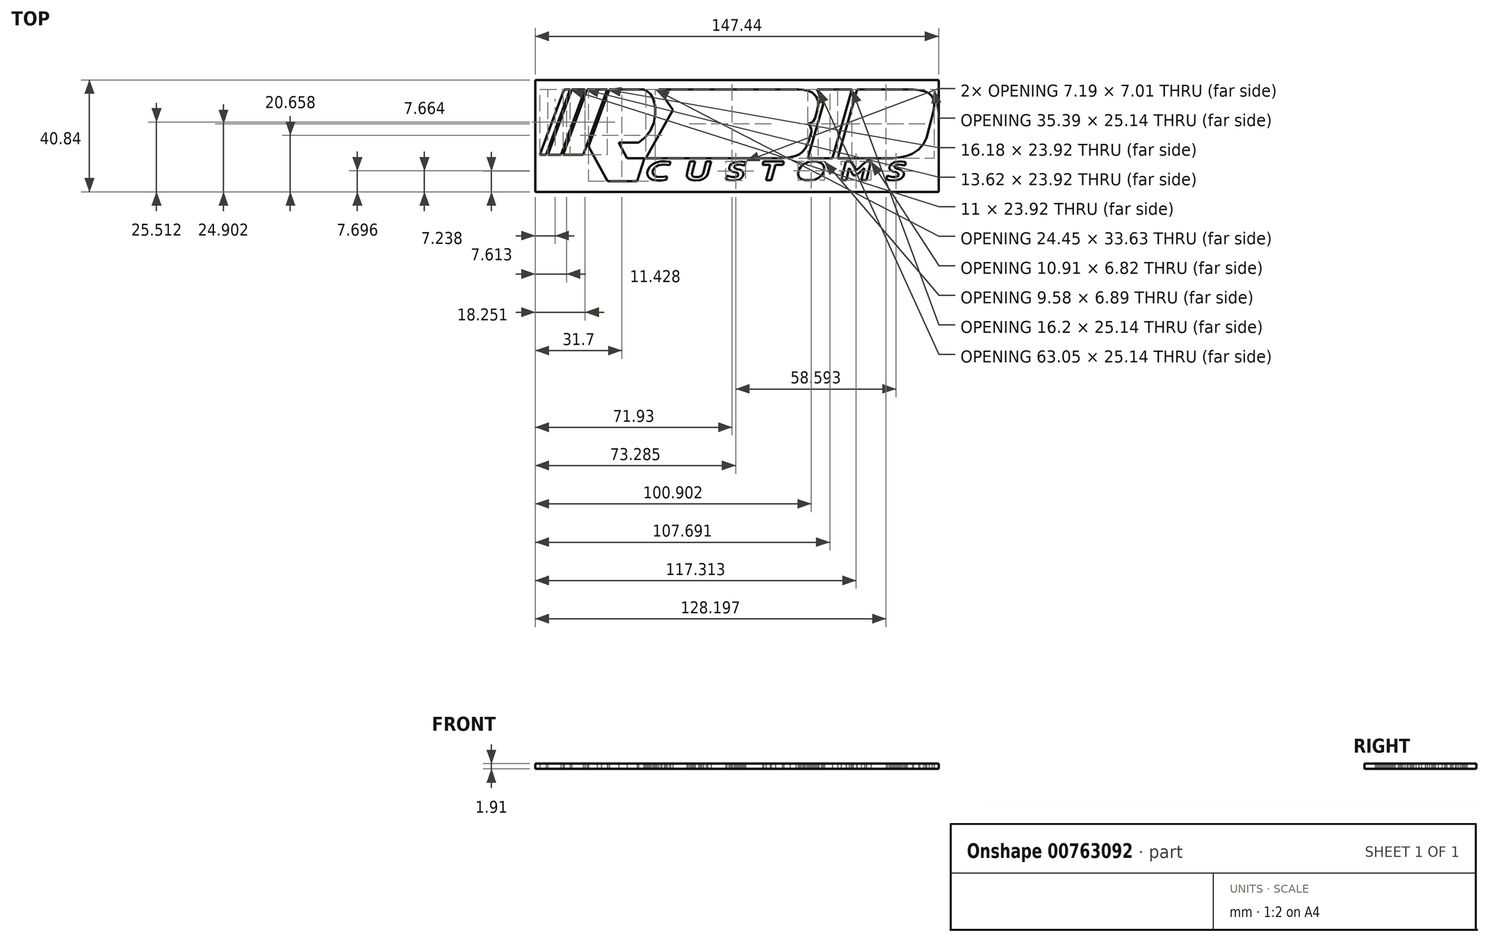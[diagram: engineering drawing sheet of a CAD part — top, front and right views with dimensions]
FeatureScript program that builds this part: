
annotation { "Feature Type Name" : "Feature", "Feature Type Description" : "" }
export const myFeature = defineFeature(function(context is Context, id is Id, definition is map)
    precondition{}
    {
        {
            var Q0;
            Q0=qCreatedBy(makeId("Top.planeOp"),FACE);
            var sketch = newSketch(context, id + "F0", { "sketchPlane" : qUnion([Q0])});
            skLineSegment(sketch, "E0", {"start": v(40.42, -9.55) * mm, "end": v(42.26, -9.55) * mm});
            skLineSegment(sketch, "E1", {"start": v(46.05, -16.37) * mm, "end": v(47.89, -16.37) * mm});
            skLineSegment(sketch, "E2", {"start": v(47.82, -9.55) * mm, "end": v(49.6, -9.55) * mm});
            skLineSegment(sketch, "E3", {"start": v(47.16, -11.96) * mm, "end": v(46.05, -16.37) * mm});
            skLineSegment(sketch, "E4", {"start": v(44.27, -14.59) * mm, "end": v(47.16, -11.96) * mm});
            skLineSegment(sketch, "E5", {"start": v(43.16, -14.59) * mm, "end": v(44.27, -14.59) * mm});
            skLineSegment(sketch, "E6", {"start": v(41.6, -11.98) * mm, "end": v(43.16, -14.59) * mm});
            skLineSegment(sketch, "E7", {"start": v(49.6, -9.55) * mm, "end": v(47.89, -16.37) * mm});
            skLineSegment(sketch, "E8", {"start": v(44.21, -12.83) * mm, "end": v(47.82, -9.55) * mm});
            skLineSegment(sketch, "E9", {"start": v(42.26, -9.55) * mm, "end": v(44.21, -12.83) * mm});
            skLineSegment(sketch, "E10", {"start": v(41.6, -11.98) * mm, "end": v(40.5, -16.37) * mm});
            skLineSegment(sketch, "E11", {"start": v(40.42, -9.55) * mm, "end": v(38.7, -16.37) * mm});
            skLineSegment(sketch, "E12", {"start": v(28.33, -9.55) * mm, "end": v(26.64, -9.76) * mm});
            skLineSegment(sketch, "E13", {"start": v(26.64, -9.76) * mm, "end": v(24.97, -10.5) * mm});
            skLineSegment(sketch, "E14", {"start": v(24.97, -10.5) * mm, "end": v(23.75, -11.65) * mm});
            skLineSegment(sketch, "E15", {"start": v(23.75, -11.65) * mm, "end": v(23.18, -12.71) * mm});
            skLineSegment(sketch, "E16", {"start": v(23.18, -12.71) * mm, "end": v(22.95, -13.91) * mm});
            skLineSegment(sketch, "E17", {"start": v(22.95, -13.91) * mm, "end": v(23.15, -15.07) * mm});
            skLineSegment(sketch, "E18", {"start": v(23.15, -15.07) * mm, "end": v(23.88, -15.86) * mm});
            skLineSegment(sketch, "E19", {"start": v(23.88, -15.86) * mm, "end": v(25.38, -16.36) * mm});
            skLineSegment(sketch, "E20", {"start": v(25.38, -16.36) * mm, "end": v(27.12, -16.44) * mm});
            skLineSegment(sketch, "E21", {"start": v(27.12, -16.44) * mm, "end": v(28.98, -16.25) * mm});
            skLineSegment(sketch, "E22", {"start": v(28.98, -16.25) * mm, "end": v(30.55, -15.5) * mm});
            skLineSegment(sketch, "E23", {"start": v(30.55, -15.5) * mm, "end": v(31.72, -14.43) * mm});
            skLineSegment(sketch, "E24", {"start": v(31.72, -14.43) * mm, "end": v(32.25, -13.43) * mm});
            skLineSegment(sketch, "E25", {"start": v(32.25, -13.43) * mm, "end": v(32.53, -12.09) * mm});
            skLineSegment(sketch, "E26", {"start": v(32.53, -12.09) * mm, "end": v(32.23, -10.87) * mm});
            skLineSegment(sketch, "E27", {"start": v(32.23, -10.87) * mm, "end": v(31.4, -10.13) * mm});
            skLineSegment(sketch, "E28", {"start": v(31.4, -10.13) * mm, "end": v(29.92, -9.63) * mm});
            skLineSegment(sketch, "E29", {"start": v(29.92, -9.63) * mm, "end": v(28.33, -9.55) * mm});
            skLineSegment(sketch, "E30", {"start": v(17.42, -10.84) * mm, "end": v(17.74, -9.55) * mm});
            skLineSegment(sketch, "E31", {"start": v(14.63, -10.84) * mm, "end": v(17.42, -10.84) * mm});
            skLineSegment(sketch, "E32", {"start": v(13.16, -16.37) * mm, "end": v(14.63, -10.84) * mm});
            skLineSegment(sketch, "E33", {"start": v(11.28, -16.37) * mm, "end": v(11.47, -16.37) * mm});
            skLineSegment(sketch, "E34", {"start": v(12.75, -10.84) * mm, "end": v(11.28, -16.37) * mm});
            skLineSegment(sketch, "E35", {"start": v(9.96, -10.84) * mm, "end": v(12.75, -10.84) * mm});
            skLineSegment(sketch, "E36", {"start": v(10.28, -9.55) * mm, "end": v(9.96, -10.84) * mm});
            skLineSegment(sketch, "E37", {"start": v(55.5, -14.69) * mm, "end": v(55.12, -16.02) * mm});
            skLineSegment(sketch, "E38", {"start": v(62.31, -9.82) * mm, "end": v(60.42, -9.53) * mm});
            skLineSegment(sketch, "E39", {"start": v(60.42, -9.53) * mm, "end": v(58.37, -9.72) * mm});
            skLineSegment(sketch, "E40", {"start": v(58.37, -9.72) * mm, "end": v(56.95, -10.49) * mm});
            skLineSegment(sketch, "E41", {"start": v(56.95, -10.49) * mm, "end": v(56.44, -11.2) * mm});
            skLineSegment(sketch, "E42", {"start": v(56.44, -11.2) * mm, "end": v(56.3, -12.06) * mm});
            skLineSegment(sketch, "E43", {"start": v(56.3, -12.06) * mm, "end": v(56.52, -12.6) * mm});
            skLineSegment(sketch, "E44", {"start": v(56.52, -12.6) * mm, "end": v(57.02, -12.95) * mm});
            skLineSegment(sketch, "E45", {"start": v(57.02, -12.95) * mm, "end": v(57.56, -13.17) * mm});
            skLineSegment(sketch, "E46", {"start": v(57.56, -13.17) * mm, "end": v(58.24, -13.4) * mm});
            skLineSegment(sketch, "E47", {"start": v(58.24, -13.4) * mm, "end": v(58.94, -13.62) * mm});
            skLineSegment(sketch, "E48", {"start": v(58.94, -13.62) * mm, "end": v(59.4, -13.82) * mm});
            skLineSegment(sketch, "E49", {"start": v(59.4, -13.82) * mm, "end": v(59.67, -14.18) * mm});
            skLineSegment(sketch, "E50", {"start": v(59.67, -14.18) * mm, "end": v(59.68, -14.56) * mm});
            skLineSegment(sketch, "E51", {"start": v(59.68, -14.56) * mm, "end": v(59.34, -14.98) * mm});
            skLineSegment(sketch, "E52", {"start": v(59.34, -14.98) * mm, "end": v(58.5, -15.25) * mm});
            skLineSegment(sketch, "E53", {"start": v(58.5, -15.25) * mm, "end": v(57.48, -15.22) * mm});
            skLineSegment(sketch, "E54", {"start": v(57.48, -15.22) * mm, "end": v(56.34, -15.01) * mm});
            skLineSegment(sketch, "E55", {"start": v(56.34, -15.01) * mm, "end": v(55.5, -14.69) * mm});
            skLineSegment(sketch, "E56", {"start": v(62.05, -11.04) * mm, "end": v(60.8, -10.76) * mm});
            skLineSegment(sketch, "E57", {"start": v(60.8, -10.76) * mm, "end": v(59.61, -10.67) * mm});
            skLineSegment(sketch, "E58", {"start": v(59.61, -10.67) * mm, "end": v(58.6, -10.88) * mm});
            skLineSegment(sketch, "E59", {"start": v(58.6, -10.88) * mm, "end": v(58.19, -11.37) * mm});
            skLineSegment(sketch, "E60", {"start": v(58.19, -11.37) * mm, "end": v(58.28, -11.84) * mm});
            skLineSegment(sketch, "E61", {"start": v(58.28, -11.84) * mm, "end": v(58.79, -12.13) * mm});
            skLineSegment(sketch, "E62", {"start": v(58.79, -12.13) * mm, "end": v(59.58, -12.38) * mm});
            skLineSegment(sketch, "E63", {"start": v(59.58, -12.38) * mm, "end": v(60.29, -12.61) * mm});
            skLineSegment(sketch, "E64", {"start": v(60.29, -12.61) * mm, "end": v(60.77, -12.83) * mm});
            skLineSegment(sketch, "E65", {"start": v(60.77, -12.83) * mm, "end": v(61.5, -13.41) * mm});
            skLineSegment(sketch, "E66", {"start": v(61.5, -13.41) * mm, "end": v(61.6, -14.2) * mm});
            skLineSegment(sketch, "E67", {"start": v(61.6, -14.2) * mm, "end": v(61.33, -15.03) * mm});
            skLineSegment(sketch, "E68", {"start": v(61.33, -15.03) * mm, "end": v(60.68, -15.74) * mm});
            skLineSegment(sketch, "E69", {"start": v(60.68, -15.74) * mm, "end": v(59.85, -16.19) * mm});
            skLineSegment(sketch, "E70", {"start": v(59.85, -16.19) * mm, "end": v(58.8, -16.44) * mm});
            skLineSegment(sketch, "E71", {"start": v(58.8, -16.44) * mm, "end": v(57.5, -16.54) * mm});
            skLineSegment(sketch, "E72", {"start": v(57.5, -16.54) * mm, "end": v(56.2, -16.35) * mm});
            skLineSegment(sketch, "E73", {"start": v(56.2, -16.35) * mm, "end": v(55.12, -16.02) * mm});
            skLineSegment(sketch, "E74", {"start": v(62.31, -9.82) * mm, "end": v(62.05, -11.04) * mm});
            skLineSegment(sketch, "E75", {"start": v(-3.1, -14.7) * mm, "end": v(-3.47, -16.03) * mm});
            skLineSegment(sketch, "E76", {"start": v(3.72, -9.83) * mm, "end": v(1.82, -9.54) * mm});
            skLineSegment(sketch, "E77", {"start": v(1.82, -9.54) * mm, "end": v(-0.22, -9.73) * mm});
            skLineSegment(sketch, "E78", {"start": v(-0.22, -9.73) * mm, "end": v(-1.65, -10.5) * mm});
            skLineSegment(sketch, "E79", {"start": v(-1.65, -10.5) * mm, "end": v(-2.15, -11.2) * mm});
            skLineSegment(sketch, "E80", {"start": v(-2.15, -11.2) * mm, "end": v(-2.3, -12.06) * mm});
            skLineSegment(sketch, "E81", {"start": v(-2.3, -12.06) * mm, "end": v(-2.07, -12.61) * mm});
            skLineSegment(sketch, "E82", {"start": v(-2.07, -12.61) * mm, "end": v(-1.57, -12.96) * mm});
            skLineSegment(sketch, "E83", {"start": v(-1.57, -12.96) * mm, "end": v(-1.04, -13.18) * mm});
            skLineSegment(sketch, "E84", {"start": v(-1.04, -13.18) * mm, "end": v(-0.35, -13.4) * mm});
            skLineSegment(sketch, "E85", {"start": v(-0.35, -13.4) * mm, "end": v(0.34, -13.63) * mm});
            skLineSegment(sketch, "E86", {"start": v(0.34, -13.63) * mm, "end": v(0.8, -13.83) * mm});
            skLineSegment(sketch, "E87", {"start": v(0.8, -13.83) * mm, "end": v(1.08, -14.19) * mm});
            skLineSegment(sketch, "E88", {"start": v(1.08, -14.19) * mm, "end": v(1.08, -14.57) * mm});
            skLineSegment(sketch, "E89", {"start": v(1.08, -14.57) * mm, "end": v(0.75, -15) * mm});
            skLineSegment(sketch, "E90", {"start": v(0.75, -15) * mm, "end": v(-0.1, -15.26) * mm});
            skLineSegment(sketch, "E91", {"start": v(-0.1, -15.26) * mm, "end": v(-1.11, -15.23) * mm});
            skLineSegment(sketch, "E92", {"start": v(-1.11, -15.23) * mm, "end": v(-2.25, -15.02) * mm});
            skLineSegment(sketch, "E93", {"start": v(-2.25, -15.02) * mm, "end": v(-3.1, -14.7) * mm});
            skLineSegment(sketch, "E94", {"start": v(3.46, -11.04) * mm, "end": v(2.2, -10.77) * mm});
            skLineSegment(sketch, "E95", {"start": v(2.2, -10.77) * mm, "end": v(1.02, -10.68) * mm});
            skLineSegment(sketch, "E96", {"start": v(1.02, -10.68) * mm, "end": v(0.02, -10.89) * mm});
            skLineSegment(sketch, "E97", {"start": v(0.02, -10.89) * mm, "end": v(-0.4, -11.38) * mm});
            skLineSegment(sketch, "E98", {"start": v(-0.4, -11.38) * mm, "end": v(-0.31, -11.85) * mm});
            skLineSegment(sketch, "E99", {"start": v(-0.31, -11.85) * mm, "end": v(0.2, -12.14) * mm});
            skLineSegment(sketch, "E100", {"start": v(0.2, -12.14) * mm, "end": v(0.99, -12.4) * mm});
            skLineSegment(sketch, "E101", {"start": v(0.99, -12.4) * mm, "end": v(1.7, -12.62) * mm});
            skLineSegment(sketch, "E102", {"start": v(1.7, -12.62) * mm, "end": v(2.18, -12.84) * mm});
            skLineSegment(sketch, "E103", {"start": v(2.18, -12.84) * mm, "end": v(2.9, -13.42) * mm});
            skLineSegment(sketch, "E104", {"start": v(2.9, -13.42) * mm, "end": v(3, -14.21) * mm});
            skLineSegment(sketch, "E105", {"start": v(3, -14.21) * mm, "end": v(2.73, -15.04) * mm});
            skLineSegment(sketch, "E106", {"start": v(2.73, -15.04) * mm, "end": v(2.08, -15.75) * mm});
            skLineSegment(sketch, "E107", {"start": v(2.08, -15.75) * mm, "end": v(1.25, -16.2) * mm});
            skLineSegment(sketch, "E108", {"start": v(1.25, -16.2) * mm, "end": v(0.2, -16.45) * mm});
            skLineSegment(sketch, "E109", {"start": v(0.2, -16.45) * mm, "end": v(-1.08, -16.55) * mm});
            skLineSegment(sketch, "E110", {"start": v(-1.08, -16.55) * mm, "end": v(-2.4, -16.36) * mm});
            skLineSegment(sketch, "E111", {"start": v(-2.4, -16.36) * mm, "end": v(-3.47, -16.03) * mm});
            skLineSegment(sketch, "E112", {"start": v(3.72, -9.83) * mm, "end": v(3.46, -11.04) * mm});
            skLineSegment(sketch, "E113", {"start": v(-10.66, -9.55) * mm, "end": v(-8.86, -9.55) * mm});
            skLineSegment(sketch, "E114", {"start": v(-15.84, -13.84) * mm, "end": v(-15.9, -14.3) * mm});
            skLineSegment(sketch, "E115", {"start": v(-15.9, -14.3) * mm, "end": v(-15.74, -14.76) * mm});
            skLineSegment(sketch, "E116", {"start": v(-15.74, -14.76) * mm, "end": v(-15.37, -15.07) * mm});
            skLineSegment(sketch, "E117", {"start": v(-15.37, -15.07) * mm, "end": v(-14.82, -15.24) * mm});
            skLineSegment(sketch, "E118", {"start": v(-14.82, -15.24) * mm, "end": v(-13.42, -15.23) * mm});
            skLineSegment(sketch, "E119", {"start": v(-13.42, -15.23) * mm, "end": v(-12.35, -14.87) * mm});
            skLineSegment(sketch, "E120", {"start": v(-12.35, -14.87) * mm, "end": v(-11.82, -14.03) * mm});
            skLineSegment(sketch, "E121", {"start": v(-17.67, -13.74) * mm, "end": v(-17.74, -14.84) * mm});
            skLineSegment(sketch, "E122", {"start": v(-17.74, -14.84) * mm, "end": v(-17.26, -15.76) * mm});
            skLineSegment(sketch, "E123", {"start": v(-17.26, -15.76) * mm, "end": v(-16.24, -16.3) * mm});
            skLineSegment(sketch, "E124", {"start": v(-16.24, -16.3) * mm, "end": v(-14.86, -16.5) * mm});
            skLineSegment(sketch, "E125", {"start": v(-14.86, -16.5) * mm, "end": v(-12.9, -16.4) * mm});
            skLineSegment(sketch, "E126", {"start": v(-12.9, -16.4) * mm, "end": v(-11.66, -15.9) * mm});
            skLineSegment(sketch, "E127", {"start": v(-11.66, -15.9) * mm, "end": v(-10.58, -15.08) * mm});
            skLineSegment(sketch, "E128", {"start": v(-10.58, -15.08) * mm, "end": v(-10.05, -14.17) * mm});
            skLineSegment(sketch, "E129", {"start": v(-8.86, -9.55) * mm, "end": v(-10.05, -14.17) * mm});
            skLineSegment(sketch, "E130", {"start": v(-10.66, -9.55) * mm, "end": v(-11.82, -14.03) * mm});
            skLineSegment(sketch, "E131", {"start": v(-14.73, -9.55) * mm, "end": v(-15.84, -13.84) * mm});
            skLineSegment(sketch, "E132", {"start": v(-16.58, -9.55) * mm, "end": v(-17.67, -13.74) * mm});
            skLineSegment(sketch, "E133", {"start": v(11.47, -16.37) * mm, "end": v(13.16, -16.37) * mm});
            skLineSegment(sketch, "E134", {"start": v(-16.58, -9.55) * mm, "end": v(-14.73, -9.55) * mm});
            skLineSegment(sketch, "E135", {"start": v(-24.91, -15.04) * mm, "end": v(-25.17, -16.21) * mm});
            skLineSegment(sketch, "E136", {"start": v(-23.75, -9.7) * mm, "end": v(-25.46, -9.49) * mm});
            skLineSegment(sketch, "E137", {"start": v(-25.46, -9.49) * mm, "end": v(-27.31, -9.52) * mm});
            skLineSegment(sketch, "E138", {"start": v(-27.31, -9.52) * mm, "end": v(-29.2, -10.02) * mm});
            skLineSegment(sketch, "E139", {"start": v(-29.2, -10.02) * mm, "end": v(-30.33, -10.61) * mm});
            skLineSegment(sketch, "E140", {"start": v(-30.33, -10.61) * mm, "end": v(-31.37, -11.6) * mm});
            skLineSegment(sketch, "E141", {"start": v(-31.37, -11.6) * mm, "end": v(-31.97, -12.67) * mm});
            skLineSegment(sketch, "E142", {"start": v(-31.97, -12.67) * mm, "end": v(-32.2, -13.7) * mm});
            skLineSegment(sketch, "E143", {"start": v(-32.2, -13.7) * mm, "end": v(-32.1, -14.5) * mm});
            skLineSegment(sketch, "E144", {"start": v(-32.1, -14.5) * mm, "end": v(-31.75, -15.24) * mm});
            skLineSegment(sketch, "E145", {"start": v(-31.75, -15.24) * mm, "end": v(-31.15, -15.81) * mm});
            skLineSegment(sketch, "E146", {"start": v(-31.15, -15.81) * mm, "end": v(-30.33, -16.2) * mm});
            skLineSegment(sketch, "E147", {"start": v(-30.33, -16.2) * mm, "end": v(-28.66, -16.51) * mm});
            skLineSegment(sketch, "E148", {"start": v(-28.66, -16.51) * mm, "end": v(-26.83, -16.51) * mm});
            skLineSegment(sketch, "E149", {"start": v(-26.83, -16.51) * mm, "end": v(-25.17, -16.21) * mm});
            skLineSegment(sketch, "E150", {"start": v(-24.03, -10.99) * mm, "end": v(-26.03, -10.68) * mm});
            skLineSegment(sketch, "E151", {"start": v(-26.03, -10.68) * mm, "end": v(-28.04, -10.96) * mm});
            skLineSegment(sketch, "E152", {"start": v(-28.04, -10.96) * mm, "end": v(-29.02, -11.46) * mm});
            skLineSegment(sketch, "E153", {"start": v(-29.02, -11.46) * mm, "end": v(-29.77, -12.2) * mm});
            skLineSegment(sketch, "E154", {"start": v(-29.77, -12.2) * mm, "end": v(-30.16, -12.97) * mm});
            skLineSegment(sketch, "E155", {"start": v(-30.16, -12.97) * mm, "end": v(-30.23, -13.75) * mm});
            skLineSegment(sketch, "E156", {"start": v(-30.23, -13.75) * mm, "end": v(-29.78, -14.65) * mm});
            skLineSegment(sketch, "E157", {"start": v(-29.78, -14.65) * mm, "end": v(-28.8, -15.1) * mm});
            skLineSegment(sketch, "E158", {"start": v(-28.8, -15.1) * mm, "end": v(-26.94, -15.3) * mm});
            skLineSegment(sketch, "E159", {"start": v(-26.94, -15.3) * mm, "end": v(-24.91, -15.04) * mm});
            skLineSegment(sketch, "E160", {"start": v(-23.75, -9.7) * mm, "end": v(-24.03, -10.99) * mm});
            skLineSegment(sketch, "E161", {"start": v(69.84, -0.9) * mm, "end": v(68.76, -3.12) * mm});
            skLineSegment(sketch, "E162", {"start": v(68.76, -3.12) * mm, "end": v(67, -5.17) * mm});
            skLineSegment(sketch, "E163", {"start": v(67, -5.17) * mm, "end": v(64.73, -6.7) * mm});
            skLineSegment(sketch, "E164", {"start": v(64.73, -6.7) * mm, "end": v(62.78, -7.48) * mm});
            skLineSegment(sketch, "E165", {"start": v(62.78, -7.48) * mm, "end": v(60.46, -8.02) * mm});
            skLineSegment(sketch, "E166", {"start": v(60.46, -8.02) * mm, "end": v(57.74, -8.33) * mm});
            skLineSegment(sketch, "E167", {"start": v(42.63, 16.81) * mm, "end": v(29.83, 16.81) * mm});
            skLineSegment(sketch, "E168", {"start": v(37.34, -8.33) * mm, "end": v(57.74, -8.33) * mm});
            skLineSegment(sketch, "E169", {"start": v(26.43, -8.33) * mm, "end": v(35.44, -8.33) * mm});
            skLineSegment(sketch, "E170", {"start": v(23.18, 16.81) * mm, "end": v(-0.77, 16.81) * mm});
            skLineSegment(sketch, "E171", {"start": v(-8.5, 16.81) * mm, "end": v(-28.07, 16.81) * mm});
            skLineSegment(sketch, "E172", {"start": v(2.73, -8.33) * mm, "end": v(17.25, -8.33) * mm});
            skLineSegment(sketch, "E173", {"start": v(-22.78, 9.31) * mm, "end": v(-32.76, -8.33) * mm});
            skLineSegment(sketch, "E174", {"start": v(29.83, 16.81) * mm, "end": v(32.18, 11.5) * mm});
            skLineSegment(sketch, "E175", {"start": v(32.18, 11.5) * mm, "end": v(26.43, -8.33) * mm});
            skLineSegment(sketch, "E176", {"start": v(42.63, 16.81) * mm, "end": v(35.44, -8.33) * mm});
            skLineSegment(sketch, "E177", {"start": v(44.53, 16.81) * mm, "end": v(37.34, -8.33) * mm});
            skLineSegment(sketch, "E178", {"start": v(72.6, 9.4) * mm, "end": v(72.73, 11.14) * mm});
            skLineSegment(sketch, "E179", {"start": v(72.73, 11.14) * mm, "end": v(72.5, 12.82) * mm});
            skLineSegment(sketch, "E180", {"start": v(72.5, 12.82) * mm, "end": v(71.77, 14.33) * mm});
            skLineSegment(sketch, "E181", {"start": v(71.77, 14.33) * mm, "end": v(70.74, 15.37) * mm});
            skLineSegment(sketch, "E182", {"start": v(70.74, 15.37) * mm, "end": v(69.33, 16.02) * mm});
            skLineSegment(sketch, "E183", {"start": v(69.33, 16.02) * mm, "end": v(67.4, 16.56) * mm});
            skLineSegment(sketch, "E184", {"start": v(67.4, 16.56) * mm, "end": v(65.13, 16.81) * mm});
            skLineSegment(sketch, "E185", {"start": v(72.6, 9.4) * mm, "end": v(69.84, -0.9) * mm});
            skLineSegment(sketch, "E186", {"start": v(26.33, 4.26) * mm, "end": v(27.18, 4.4) * mm});
            skLineSegment(sketch, "E187", {"start": v(27.18, 4.4) * mm, "end": v(27.93, 4.66) * mm});
            skLineSegment(sketch, "E188", {"start": v(27.93, 4.66) * mm, "end": v(28.5, 5.19) * mm});
            skLineSegment(sketch, "E189", {"start": v(28.5, 5.19) * mm, "end": v(29.07, 6.28) * mm});
            skLineSegment(sketch, "E190", {"start": v(29.07, 6.28) * mm, "end": v(29.82, 8.46) * mm});
            skLineSegment(sketch, "E191", {"start": v(29.82, 8.46) * mm, "end": v(30.3, 10.75) * mm});
            skLineSegment(sketch, "E192", {"start": v(30.3, 10.75) * mm, "end": v(30.27, 12.45) * mm});
            skLineSegment(sketch, "E193", {"start": v(30.27, 12.45) * mm, "end": v(29.52, 14.24) * mm});
            skLineSegment(sketch, "E194", {"start": v(29.52, 14.24) * mm, "end": v(28.06, 15.6) * mm});
            skLineSegment(sketch, "E195", {"start": v(28.06, 15.6) * mm, "end": v(26.62, 16.23) * mm});
            skLineSegment(sketch, "E196", {"start": v(26.62, 16.23) * mm, "end": v(24.88, 16.66) * mm});
            skLineSegment(sketch, "E197", {"start": v(24.88, 16.66) * mm, "end": v(23.18, 16.81) * mm});
            skLineSegment(sketch, "E198", {"start": v(26.33, 4.26) * mm, "end": v(26.98, 3.8) * mm});
            skLineSegment(sketch, "E199", {"start": v(26.98, 3.8) * mm, "end": v(27.5, 3.08) * mm});
            skLineSegment(sketch, "E200", {"start": v(27.5, 3.08) * mm, "end": v(27.8, 2.23) * mm});
            skLineSegment(sketch, "E201", {"start": v(27.8, 2.23) * mm, "end": v(27.8, 1.48) * mm});
            skLineSegment(sketch, "E202", {"start": v(27.8, 1.48) * mm, "end": v(27.47, 0.1) * mm});
            skLineSegment(sketch, "E203", {"start": v(27.47, 0.1) * mm, "end": v(26.82, -1.9) * mm});
            skLineSegment(sketch, "E204", {"start": v(26.82, -1.9) * mm, "end": v(26.2, -3.5) * mm});
            skLineSegment(sketch, "E205", {"start": v(26.2, -3.5) * mm, "end": v(25.56, -4.77) * mm});
            skLineSegment(sketch, "E206", {"start": v(25.56, -4.77) * mm, "end": v(24.6, -5.92) * mm});
            skLineSegment(sketch, "E207", {"start": v(24.6, -5.92) * mm, "end": v(23.49, -6.81) * mm});
            skLineSegment(sketch, "E208", {"start": v(23.49, -6.81) * mm, "end": v(22.2, -7.5) * mm});
            skLineSegment(sketch, "E209", {"start": v(22.2, -7.5) * mm, "end": v(19.95, -8) * mm});
            skLineSegment(sketch, "E210", {"start": v(19.95, -8) * mm, "end": v(17.25, -8.33) * mm});
            skLineSegment(sketch, "E211", {"start": v(-33.51, 16.81) * mm, "end": v(-32.12, 16.04) * mm});
            skLineSegment(sketch, "E212", {"start": v(-32.12, 16.04) * mm, "end": v(-30.97, 14.97) * mm});
            skLineSegment(sketch, "E213", {"start": v(-30.97, 14.97) * mm, "end": v(-30.1, 13.47) * mm});
            skLineSegment(sketch, "E214", {"start": v(-30.1, 13.47) * mm, "end": v(-29.23, 10.61) * mm});
            skLineSegment(sketch, "E215", {"start": v(-29.23, 10.61) * mm, "end": v(-29.24, 7.62) * mm});
            skLineSegment(sketch, "E216", {"start": v(-29.24, 7.62) * mm, "end": v(-29.86, 4.52) * mm});
            skLineSegment(sketch, "E217", {"start": v(-29.86, 4.52) * mm, "end": v(-31.1, 1.59) * mm});
            skLineSegment(sketch, "E218", {"start": v(-31.1, 1.59) * mm, "end": v(-33.02, -0.8) * mm});
            skLineSegment(sketch, "E219", {"start": v(-33.02, -0.8) * mm, "end": v(-35.37, -2.66) * mm});
            skLineSegment(sketch, "E220", {"start": v(-33.51, 16.81) * mm, "end": v(-46.1, 16.81) * mm});
            skLineSegment(sketch, "E221", {"start": v(-5.07, -8.33) * mm, "end": v(2.3, -8.33) * mm});
            skLineSegment(sketch, "E222", {"start": v(38.7, -16.37) * mm, "end": v(40.5, -16.37) * mm});
            skLineSegment(sketch, "E223", {"start": v(28.33, -9.55) * mm, "end": v(29.1, -9.55) * mm});
            skLineSegment(sketch, "E224", {"start": v(10.28, -9.55) * mm, "end": v(17.74, -9.55) * mm});
            skLineSegment(sketch, "E225", {"start": v(1.03, -9.55) * mm, "end": v(2.06, -9.55) * mm});
            skLineSegment(sketch, "E226", {"start": v(65.13, 16.81) * mm, "end": v(44.53, 16.81) * mm});
            skLineSegment(sketch, "E227", {"start": v(-49, 8.95) * mm, "end": v(-46.1, 16.81) * mm});
            skLineSegment(sketch, "E228", {"start": v(-50.53, 4.54) * mm, "end": v(-53.69, -4.04) * mm});
            skLineSegment(sketch, "E229", {"start": v(-53.69, -4.04) * mm, "end": v(-46.73, -16.81) * mm});
            skLineSegment(sketch, "E230", {"start": v(-46.73, -16.81) * mm, "end": v(-35.85, -16.81) * mm});
            skLineSegment(sketch, "E231", {"start": v(-35.85, -16.81) * mm, "end": v(-33.28, -8.33) * mm});
            skLineSegment(sketch, "E232", {"start": v(-33.28, -8.33) * mm, "end": v(-39.56, -8.33) * mm});
            skLineSegment(sketch, "E233", {"start": v(-39.56, -8.33) * mm, "end": v(-42.64, -2.66) * mm});
            skLineSegment(sketch, "E234", {"start": v(-42.64, -2.66) * mm, "end": v(-35.37, -2.66) * mm});
            skLineSegment(sketch, "E235", {"start": v(-32.76, -8.33) * mm, "end": v(-22.07, -8.33) * mm});
            skLineSegment(sketch, "E236", {"start": v(-28.07, 16.81) * mm, "end": v(-22.78, 9.31) * mm});
            skLineSegment(sketch, "E237", {"start": v(-22.07, -8.33) * mm, "end": v(-5.07, -8.33) * mm});
            skLineSegment(sketch, "E238", {"start": v(-49, 8.95) * mm, "end": v(-50.53, 4.54) * mm});
            skLineSegment(sketch, "E239", {"start": v(-8.5, 16.81) * mm, "end": v(-0.77, 16.81) * mm});
            skLineSegment(sketch, "E240", {"start": v(2.3, -8.33) * mm, "end": v(2.73, -8.33) * mm});
            skLineSegment(sketch, "E241", {"start": v(-71.42, -7.1) * mm, "end": v(-62.62, 16.81) * mm});
            skLineSegment(sketch, "E242", {"start": v(-55.62, -7.1) * mm, "end": v(-63, -7.1) * mm});
            skLineSegment(sketch, "E243", {"start": v(-60.42, 16.81) * mm, "end": v(-69.22, -7.1) * mm});
            skLineSegment(sketch, "E244", {"start": v(-68.54, -7.1) * mm, "end": v(-59.74, 16.81) * mm});
            skLineSegment(sketch, "E245", {"start": v(-54.92, 16.81) * mm, "end": v(-63.73, -7.1) * mm});
            skLineSegment(sketch, "E246", {"start": v(-63, -7.1) * mm, "end": v(-54.2, 16.81) * mm});
            skLineSegment(sketch, "E247", {"start": v(-46.82, 16.81) * mm, "end": v(-55.62, -7.1) * mm});
            skLineSegment(sketch, "E248.trimOffspring", {"start": v(-60.42, 16.81) * mm, "end": v(-62.62, 16.81) * mm});
            skLineSegment(sketch, "E249.trimOffspring", {"start": v(-54.92, 16.81) * mm, "end": v(-59.74, 16.81) * mm});
            skLineSegment(sketch, "E250.trimOffspring", {"start": v(-46.82, 16.81) * mm, "end": v(-54.2, 16.81) * mm});
            skLineSegment(sketch, "E251.trimOffspring", {"start": v(-63.73, -7.1) * mm, "end": v(-68.54, -7.1) * mm});
            skLineSegment(sketch, "E252.trimOffspring", {"start": v(-69.22, -7.1) * mm, "end": v(-71.42, -7.1) * mm});
            skSolve(sketch);
        }
        {
            var Q0;
            Q0=qCreatedBy(makeId("Top.planeOp"),FACE);
            var sketch = newSketch(context, id + "F1", { "sketchPlane" : qUnion([Q0])});
            skLineSegment(sketch, "E253.bottom", {"start": v(-73.16, 20.18) * mm, "end": v(74.28, 20.18) * mm});
            skLineSegment(sketch, "E253.top", {"start": v(-73.16, -20.66) * mm, "end": v(74.28, -20.66) * mm});
            skLineSegment(sketch, "E253.left", {"start": v(-73.16, 20.18) * mm, "end": v(-73.16, -20.66) * mm});
            skLineSegment(sketch, "E253.right", {"start": v(74.28, 20.18) * mm, "end": v(74.28, -20.66) * mm});
            skSolve(sketch);
        }
        {
            var Q0;
            Q0=qSketchRegion(id+"F0",true);
            var Q1;
            Q1=qSketchRegion(id+"F1",true);
            extrude(context, id + "F2", {"entities" : qUnion([Q0, Q1]), "depth" : 1.9 * mm, "offsetDistance" : 25.4 * mm});
        }
        {
            var Q0;
            Q0=qSketchRegion(id+"F0",true);
            extrude(context, id + "F3", {"entities" : qUnion([Q0]), "operationType" : NewBodyOperationType.REMOVE, "endBound" : BoundingType.THROUGH_ALL, "depth" : 25.4 * mm, "offsetDistance" : 25.4 * mm});
        }
    });
